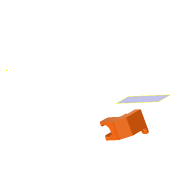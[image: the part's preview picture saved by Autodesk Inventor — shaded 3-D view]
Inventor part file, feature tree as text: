
AUTODESK INVENTOR PART (.ipt)
format: ipt  version: 2022 (Build 260153000, 153)  size: 397,312 bytes
history: native  units: in
note: dims shown in document units (in); Inventor stores cm internally (conversion verified against a paired STEP export)
features: extrude x9, sketch x9, other x8, reference x5, projected_geometry x5, fillet x2, plane x1
ambient origin geometry x8: Origin, YZ Plane, XZ Plane, XY Plane, X Axis, Y Axis, Z Axis, Center Point
bodies: Solid1 (feature_tree)
feature tree (39):
  plane  "Work Plane1"
  extrude  "Extrusion1"  Depth=0.5512in TaperAngle=0.0deg
  extrude  "Extrusion2"  Depth=0.5307in
  extrude  "Extrusion3"  TaperAngle=135.0deg  [1 undecoded]
  extrude  "Extrusion8"  Depth=0.2362in
  extrude  "Extrusion9"  Depth=0.2362in
  extrude  "Extrusion11"  Depth=0.3937in TaperAngle=0.0deg
  extrude  "Extrusion12"  Depth=0.0591in
  fillet  "Rundung1"  Radius=0.9449in
  sketch  "Skizze13"  dims[d40=0.0591in d41=0.0591in d42=0.9449in]
  extrude  "Extrusion13"  TaperAngle=0.0deg  [1 undecoded]
  extrude  "Extrusion14"  Depth=0.0394in
  fillet  "Rundung2"  Radius=0.1969in
  sketch  "Sketch2"  dims[d0=0.0591in d1=0.0in d3=0.5512in d4=0.0in]
  sketch  "Sketch3"  dims[d12=0.0591in d13=0.0in d22=0.5307in]
  reference  "Reference1"
  projected_geometry  "Projected Loop5"
  projected_geometry  "Projected Loop6"
  sketch  "Sketch8"  dims[d23=0.2653in d25=135.0deg]
  reference  "Reference2"
  reference  "Reference3"
  sketch  "Sketch9"  dims[d26=0.1575in d27=0.2362in]
  reference  "Reference4"
  sketch  "Skizze11"  dims[d28=0.1568in d29=0.2362in]
  sketch  "Skizze12"  dims[d31=0.3937in d35=0.5512in d36=0.0in]
  reference  "Referenz5"
  sketch  "Skizze14"  dims[d43=0.5512in d44=0.0in d45=0.0in]
  projected_geometry  "Projizierte Kontur8"
  projected_geometry  "Projizierte Kontur9"
  projected_geometry  "Projizierte Kontur10"
  sketch  "Skizze15"  dims[d48=0.0in d49=0.0in d50=0.315in d51=0.1969in d52=0.0in d53=0.0787in d54=0.0787in d55=0.3937in d56=0.0in d57=0.4094in d58=0.3937in d59=0.0in d60=0.0394in d61=0.0591in d62=0.0in]
  other  "<userpath>\Documents\Matchboxscope\INVENTOR\Matchboxscope_v0.iam"
  other  "Matchboxscope_v0.iam"
  other  "Matchboxscope_sample_v0:1"
  other  "Matchboxscope_middle2_v1:1"
  other  "00_ESP3-CAM:5"
  other  "Bauteil50"
  other  "Assembly_Matchboxscope_injectionmolded.iam"
  other  "IM_Matchboxscope_plate:2"
note: 2 required parameter values undecoded (feature->parameter linkage not recoverable at this tier; creation-order binding heuristic only, values carry confidence <= 0.55)
